# Revit family: svetilnik_alfresco_ar deko_dtu19
name_source: partatom
category: Lighting Fixtures
revit_build: Autodesk Revit 2016 (Build: 20150506_1715(x64)
units: mm (PartAtom-declared; Revit-internal decimal feet)

## family parameters
Always vertical = Yes
Cut with Voids When Loaded = No
Light Source = No
Part Type = Normal
Room Calculation Point = No
Round Connector Dimension = Use Diameter
Shared = No
Work Plane-Based = No

## types (4) — shared parameters
ADSK_Единица измерения = шт.
ADSK_Завод-изготовитель = ALFRESCO
ADSK_Количество фаз = 2
ADSK_Количество фаз числовое = 2
ADSK_Коэффициент мощности = 0.98
ADSK_Напряжение = 220 V
ADSK_Ток = 0 A
ADSK_Энергоэффективность = 120 lm/W
IP Class = IP 65
Manufacturer = ALFRESCO
URL = http://www.allfresco.ru
Блок аварийного питания = No
Класс защиты = 1
Класс пожароопасности = F (светильники предназначены для установки непосредственно на поверхность из нормально воспламеняемых материалов)
Климатическая зона = У1
Корпус светильника = Антрацит
Материал рассеивателя = PC
Область использования = ландшафт, коттедж. Посёлки,микрорайоны
Отражатель = Отражатель
Отступ от корпуса = 10 mm  [stored 0.0328084 ft]
Рассеиватель = Пластик
Температура эксплуатации = -40 +50
Тип ИС = LED-светодиоды
Тип КСС = Симметричная боковая
Тип ПРА = -
Тип продукции = LED-светильник
Фланец 1 = Yes
Фланец 2 = Yes
Цветовая температура = 2700-6500

## per-type parameters (varying)
| type | ADSK_Артикул | ADSK_Масса | ADSK_Модель | ADSK_Наименование | ADSK_Номинальная мощность | ADSK_Полная мощность | ADSK_Размер_Высота | ADSK_Размер_Длина | ADSK_Размер_Ширина | Apparent Load | dg | dv | dv2 | dv2/2 | Длина рассеивателя | Световой поток2 |
| ДТУ 19.0 AF | ДТУ199 | 13 | ДТУ-19.0-AF Ар-деко | Светодиодный светильник Ар-Деко ДТУ-19.0-AF-1,3Вт-1,0 | 4 W | 4 VA | 1000 mm  [stored 3.28084 ft] | 100 mm  [stored 0.328084 ft] | 100 mm  [stored 0.328084 ft] | 4 VA | 8 mm  [stored 0.0262467 ft] | 32 mm | 15 mm  [stored 0.0492126 ft] | 8 mm  [stored 0.0262467 ft] | 85 mm  [stored 0.278871 ft] | 156 lm |
| ДТУ 19.1 AF | ДТУ1911 | 34 | ДТУ-19.1-AF Ар-деко | Светодиодный светильник Ар-Деко ДТУ-19.1-AF-4Вт-1,0 | 4 W | 4 VA | 1000 mm  [stored 3.28084 ft] | 200 mm  [stored 0.656168 ft] | 160 mm  [stored 0.524934 ft] | 4 VA | 8 mm  [stored 0.0262467 ft] | 32 mm | 20 mm  [stored 0.0656168 ft] | 10 mm  [stored 0.0328084 ft] | 180 mm  [stored 0.590551 ft] | 480 lm |
| ДТУ 19.2 AF 2 | ДТУ1916 | 29 | ДТУ-19.2-AF-2 Ар-деко | Светодиодный светильник Ар-Деко ДТУ-19.2-AF-2-8Вт-0,5 | 8 W | 8 VA | 500 mm  [stored 1.64042 ft] | 280 mm  [stored 0.918635 ft] | 280 mm  [stored 0.918635 ft] | 8 VA | 8 mm  [stored 0.0262467 ft] | 32 mm | 50 mm  [stored 0.164042 ft] | 25 mm  [stored 0.082021 ft] | 230 mm  [stored 0.754593 ft] | 960 lm |
| ДТУ 19.3 AF 4 | ДТУ1920 | 31 | ДТУ-19.3-AF-4 Ар-деко | Светодиодный светильник Ар-Деко ДТУ-19.3-AF-4-16Вт-0,5 | 16 W | 16 VA | 500 mm  [stored 1.64042 ft] | 300 mm | 300 mm | 16 VA | 15 mm  [stored 0.0492126 ft] | 40 mm  [stored 0.131234 ft] | 50 mm  [stored 0.164042 ft] | 25 mm  [stored 0.082021 ft] | 250 mm  [stored 0.82021 ft] | 1920 lm |

note: [stored X ft] marks values corroborated as IEEE doubles in the binary element streams (Revit-internal decimal feet)
